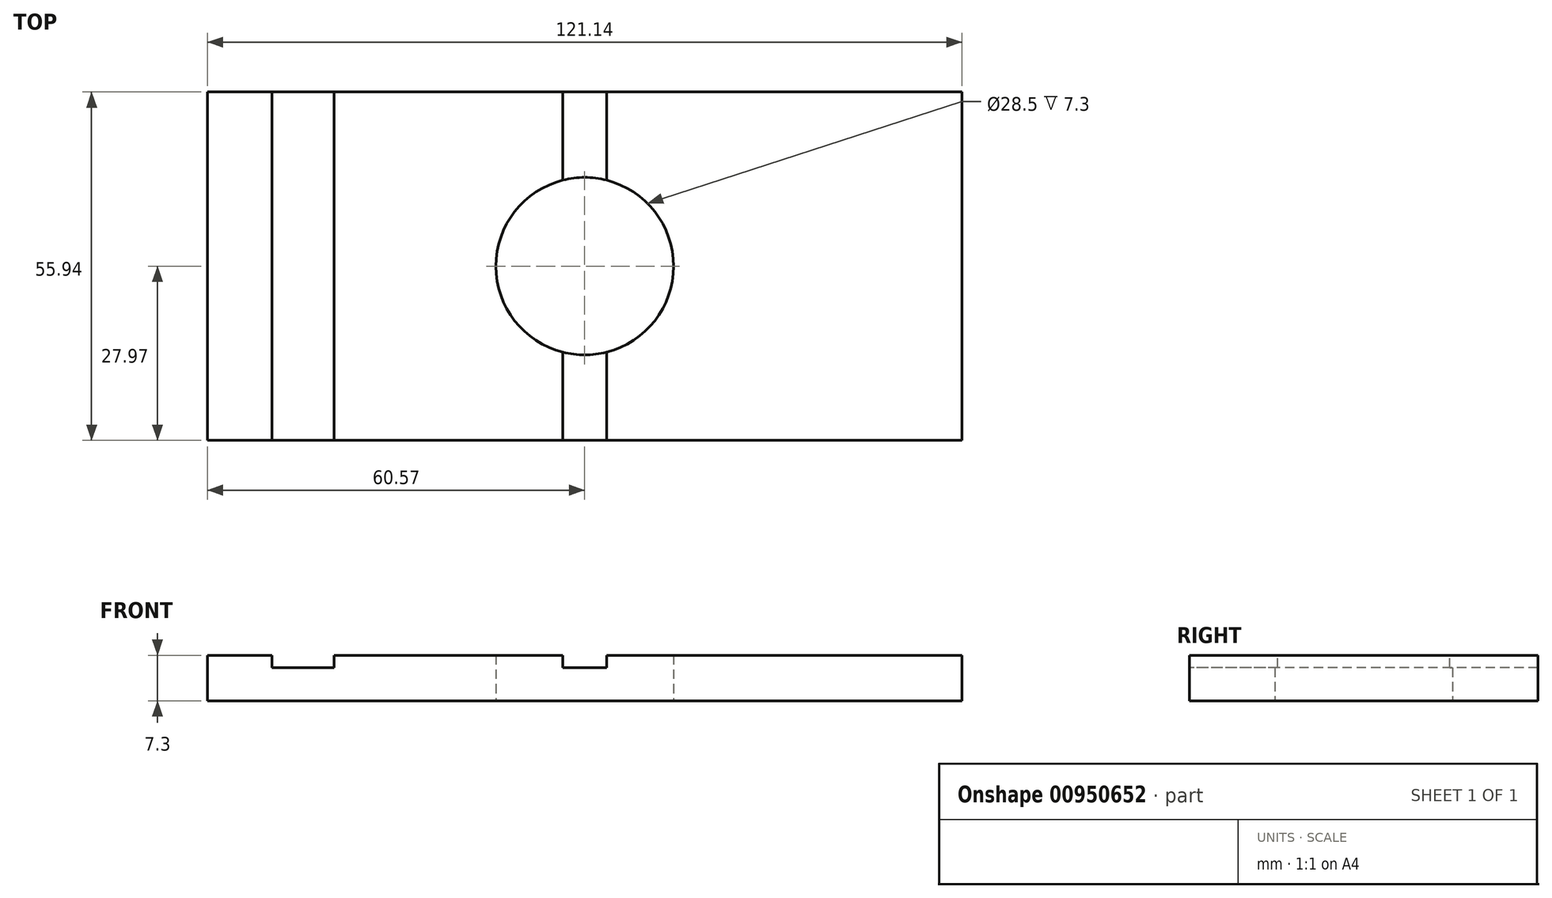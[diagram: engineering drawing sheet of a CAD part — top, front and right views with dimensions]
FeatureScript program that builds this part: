
annotation { "Feature Type Name" : "Feature", "Feature Type Description" : "" }
export const myFeature = defineFeature(function(context is Context, id is Id, definition is map)
    precondition{}
    {
        {
            var Q0;
            Q0=qCreatedBy(makeId("Top.planeOp"),FACE);
            var sketch = newSketch(context, id + "F0", { "sketchPlane" : qUnion([Q0])});
            skLineSegment(sketch, "E0.bottom", {"start": v(-60.57, -27.97) * mm, "end": v(60.57, -27.97) * mm});
            skLineSegment(sketch, "E0.top", {"start": v(-60.57, 27.97) * mm, "end": v(60.57, 27.97) * mm});
            skLineSegment(sketch, "E0.left", {"start": v(-60.57, -27.97) * mm, "end": v(-60.57, 27.97) * mm});
            skLineSegment(sketch, "E0.right", {"start": v(60.57, -27.97) * mm, "end": v(60.57, 27.97) * mm});
            skPoint(sketch, "E0.middle", {"position": v(0, 0) * mm});
            skCircle(sketch, "E1", {"center": v(0, 0) * mm, "radius": 14.25 * mm});
            skSolve(sketch);
        }
        {
            var Q0;
            Q0=makeQuery(id+"F0.imprint","IMPRINT",FACE,{"disambiguationData":[TD([[makeQuery(id+"F0.imprint","IMPRINT",EDGE,{"derivedFrom":sQuery(id+"F0.wireOp",EDGE,"E0.bottom")}),1.0]])]});
            extrude(context, id + "F1", {"entities" : qUnion([Q0]), "depth" : 7.3 * mm, "offsetDistance" : 25 * mm});
        }
        {
            var Q0;
            Q0=makeQuery(id+"F1.opExtrude","CAP_FACE",FACE,{"disambiguationData":[OSD([sQuery(id+"F0.wireOp",EDGE,"E0.bottom"),sQuery(id+"F0.wireOp",EDGE,"E0.top"),sQuery(id+"F0.wireOp",EDGE,"E0.left"),sQuery(id+"F0.wireOp",EDGE,"E0.right"),sQuery(id+"F0.wireOp",EDGE,"E1")])],"isStart":false});
            var sketch = newSketch(context, id + "F2", { "sketchPlane" : qUnion([Q0])});
            skLineSegment(sketch, "E2.bottom", {"start": v(-50.22, 27.97) * mm, "end": v(-40.22, 27.97) * mm});
            skLineSegment(sketch, "E2.top", {"start": v(-50.22, -27.97) * mm, "end": v(-40.22, -27.97) * mm});
            skLineSegment(sketch, "E2.left", {"start": v(-50.22, 27.97) * mm, "end": v(-50.22, -27.97) * mm});
            skLineSegment(sketch, "E2.right", {"start": v(-40.22, 27.97) * mm, "end": v(-40.22, -27.97) * mm});
            skLineSegment(sketch, "E3", {"start": v(-3.5, 27.97) * mm, "end": v(-3.5, -27.97) * mm});
            skLineSegment(sketch, "E4", {"start": v(3.5, 27.97) * mm, "end": v(3.5, -27.97) * mm});
            skPoint(sketch, "E5", {"position": v(0, 0) * mm});
            skLineSegment(sketch, "E6", {"start": v(-3.5, 27.97) * mm, "end": v(3.5, 27.97) * mm});
            skPoint(sketch, "E7", {"position": v(0, 27.97) * mm});
            skLineSegment(sketch, "E8", {"start": v(0, 27.97) * mm, "end": v(0, -29.41) * mm, "construction": true});
            skSolve(sketch);
        }
        {
            var Q0;
            {var subQ0=sQuery(id+"F2.wireOp",EDGE,"E6");Q0=makeQuery(id+"F2.imprint","IMPRINT",FACE,{"disambiguationData":[TD([[makeQuery(id+"F2.imprint","IMPRINT",EDGE,{"derivedFrom":subQ0}),-1.0]])]});}
            var Q1;
            {var subQ0=sQuery(id+"F2.wireOp",EDGE,"E3");var subQ1=makeQuery(id+"F1.opExtrude","CAP_EDGE",EDGE,{"disambiguationData":[OSD([sQuery(id+"F0.wireOp",EDGE,"E0.bottom")])],"isStart":false});var subQ2=makeQuery(id+"F2.imprint","INTERSECT",VERTEX,{"derivedFrom":[subQ1,subQ0]});Q1=makeQuery(id+"F2.imprint","IMPRINT",FACE,{"disambiguationData":[TD([[makeQuery(id+"F2.imprint","IMPRINT",EDGE,{"disambiguationData":[TD([[subQ2,1.0]])],"derivedFrom":subQ0}),1.0]])]});}
            var Q2;
            Q2=makeQuery(id+"F2.imprint","IMPRINT",FACE,{"disambiguationData":[TD([[makeQuery(id+"F2.imprint","IMPRINT",EDGE,{"derivedFrom":sQuery(id+"F2.wireOp",EDGE,"E2.bottom")}),-1.0]])]});
            extrude(context, id + "F3", {"entities" : qUnion([Q0, Q1, Q2]), "operationType" : NewBodyOperationType.REMOVE, "oppositeDirection" : true, "depth" : 2 * mm, "offsetDistance" : 25 * mm});
        }
    });
